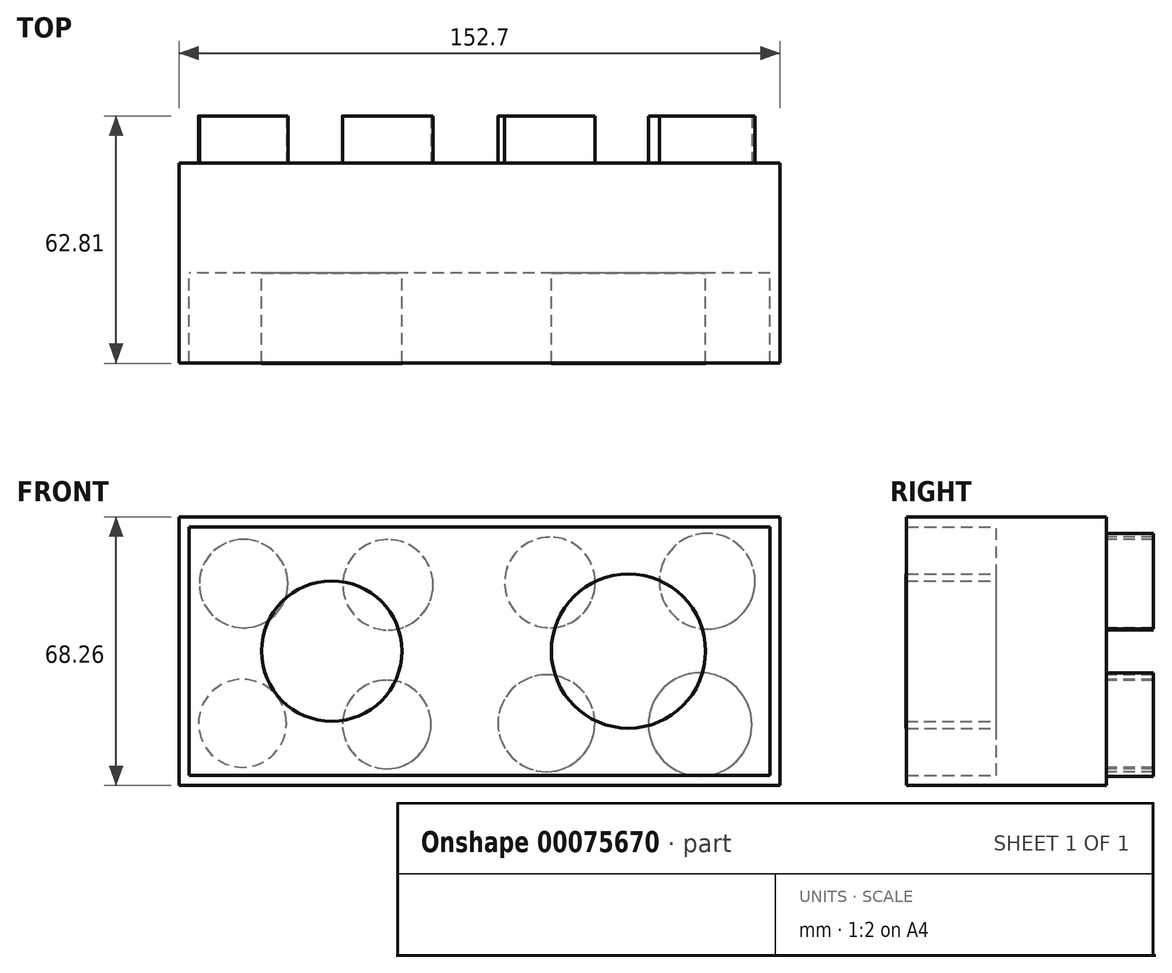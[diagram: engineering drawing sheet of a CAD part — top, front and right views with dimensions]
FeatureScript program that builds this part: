
annotation { "Feature Type Name" : "Feature", "Feature Type Description" : "" }
export const myFeature = defineFeature(function(context is Context, id is Id, definition is map)
    precondition{}
    {
        {
            var Q0;
            Q0=qCreatedBy(makeId("Front.planeOp"),FACE);
            var sketch = newSketch(context, id + "F0", { "sketchPlane" : qUnion([Q0])});
            skLineSegment(sketch, "E0.rect.bottom", {"start": v(76.35, -34.13) * mm, "end": v(-76.35, -34.13) * mm});
            skLineSegment(sketch, "E0.rect.top", {"start": v(76.35, 34.13) * mm, "end": v(-76.35, 34.13) * mm});
            skLineSegment(sketch, "E0.rect.left", {"start": v(76.35, -34.13) * mm, "end": v(76.35, 34.13) * mm});
            skLineSegment(sketch, "E0.rect.right", {"start": v(-76.35, -34.13) * mm, "end": v(-76.35, 34.13) * mm});
            skPoint(sketch, "E0.rect.middle", {"position": v(0, 0) * mm});
            skSolve(sketch);
        }
        {
            var Q0;
            Q0=makeQuery(id+"F0.imprint","IMPRINT",FACE,{"disambiguationData":[TD([[makeQuery(id+"F0.imprint","IMPRINT",EDGE,{"derivedFrom":sQuery(id+"F0.wireOp",EDGE,"E0.rect.bottom")}),-1.0]])]});
            extrude(context, id + "F1", {"entities" : qUnion([Q0]), "depth" : 25.4 * mm});
        }
        {
            var Q0;
            Q0=makeQuery(id+"F1.opExtrude","CAP_FACE",FACE,{"disambiguationData":[OSD([sQuery(id+"F0.wireOp",EDGE,"E0.rect.bottom"),sQuery(id+"F0.wireOp",EDGE,"E0.rect.top"),sQuery(id+"F0.wireOp",EDGE,"E0.rect.left"),sQuery(id+"F0.wireOp",EDGE,"E0.rect.right")])],"isStart":false});
            extrude(context, id + "F2", {"entities" : qUnion([Q0]), "operationType" : NewBodyOperationType.ADD, "depth" : 25.4 * mm});
        }
        {
            var Q0;
            Q0=makeQuery(id+"F2.opExtrude","CAP_FACE",FACE,{"disambiguationData":[OSD([sQuery(id+"F0.wireOp",EDGE,"E0.rect.bottom"),sQuery(id+"F0.wireOp",EDGE,"E0.rect.top"),sQuery(id+"F0.wireOp",EDGE,"E0.rect.left"),sQuery(id+"F0.wireOp",EDGE,"E0.rect.right")])],"isStart":false});
            shell(context, id + "F3", {"entities" : qUnion([Q0]), "thickness" : 2.54 * mm});
        }
        {
            var Q0;
            Q0=makeQuery(id+"F3.opShell","OFFSET_FACE",FACE,{"disambiguationData":[OSD([sQuery(id+"F0.wireOp",EDGE,"E0.rect.bottom"),sQuery(id+"F0.wireOp",EDGE,"E0.rect.top"),sQuery(id+"F0.wireOp",EDGE,"E0.rect.left"),sQuery(id+"F0.wireOp",EDGE,"E0.rect.right")])]});
            extrude(context, id + "F4", {"entities" : qUnion([Q0]), "operationType" : NewBodyOperationType.ADD, "depth" : 25.4 * mm});
        }
        {
            var Q0;
            Q0=makeQuery(id+"F1.opExtrude","CAP_FACE",FACE,{"disambiguationData":[OSD([sQuery(id+"F0.wireOp",EDGE,"E0.rect.bottom"),sQuery(id+"F0.wireOp",EDGE,"E0.rect.top"),sQuery(id+"F0.wireOp",EDGE,"E0.rect.left"),sQuery(id+"F0.wireOp",EDGE,"E0.rect.right")])],"isStart":true});
            var sketch = newSketch(context, id + "F5", { "sketchPlane" : qUnion([Q0])});
            skCircle(sketch, "E1", {"center": v(60.24, -18.34) * mm, "radius": 11.17 * mm});
            skCircle(sketch, "E2", {"center": v(23.56, -18.64) * mm, "radius": 11.25 * mm});
            skCircle(sketch, "E3", {"center": v(59.94, 17.15) * mm, "radius": 11.24 * mm});
            skCircle(sketch, "E4", {"center": v(23.26, 16.85) * mm, "radius": 11.47 * mm});
            skCircle(sketch, "E5", {"center": v(-17, -18.34) * mm, "radius": 12.3 * mm});
            skCircle(sketch, "E6", {"center": v(-56.06, -18.64) * mm, "radius": 13.13 * mm});
            skCircle(sketch, "E7", {"center": v(-17.9, 17.44) * mm, "radius": 11.5 * mm});
            skCircle(sketch, "E8", {"center": v(-57.85, 17.74) * mm, "radius": 12.17 * mm});
            skSolve(sketch);
        }
        {
            var Q0;
            Q0=makeQuery(id+"F5.imprint","IMPRINT",FACE,{"disambiguationData":[TD([[makeQuery(id+"F5.imprint","IMPRINT",EDGE,{"derivedFrom":sQuery(id+"F5.wireOp",EDGE,"E1")}),1.0]])]});
            var Q1;
            Q1=makeQuery(id+"F5.imprint","IMPRINT",FACE,{"disambiguationData":[TD([[makeQuery(id+"F5.imprint","IMPRINT",EDGE,{"derivedFrom":sQuery(id+"F5.wireOp",EDGE,"E2")}),1.0]])]});
            var Q2;
            Q2=makeQuery(id+"F5.imprint","IMPRINT",FACE,{"disambiguationData":[TD([[makeQuery(id+"F5.imprint","IMPRINT",EDGE,{"derivedFrom":sQuery(id+"F5.wireOp",EDGE,"E5")}),1.0]])]});
            var Q3;
            Q3=makeQuery(id+"F5.imprint","IMPRINT",FACE,{"disambiguationData":[TD([[makeQuery(id+"F5.imprint","IMPRINT",EDGE,{"derivedFrom":sQuery(id+"F5.wireOp",EDGE,"E6")}),1.0]])]});
            var Q4;
            Q4=makeQuery(id+"F5.imprint","IMPRINT",FACE,{"disambiguationData":[TD([[makeQuery(id+"F5.imprint","IMPRINT",EDGE,{"derivedFrom":sQuery(id+"F5.wireOp",EDGE,"E8")}),1.0]])]});
            var Q5;
            Q5=makeQuery(id+"F5.imprint","IMPRINT",FACE,{"disambiguationData":[TD([[makeQuery(id+"F5.imprint","IMPRINT",EDGE,{"derivedFrom":sQuery(id+"F5.wireOp",EDGE,"E7")}),1.0]])]});
            var Q6;
            Q6=makeQuery(id+"F5.imprint","IMPRINT",FACE,{"disambiguationData":[TD([[makeQuery(id+"F5.imprint","IMPRINT",EDGE,{"derivedFrom":sQuery(id+"F5.wireOp",EDGE,"E4")}),1.0]])]});
            var Q7;
            Q7=makeQuery(id+"F5.imprint","IMPRINT",FACE,{"disambiguationData":[TD([[makeQuery(id+"F5.imprint","IMPRINT",EDGE,{"derivedFrom":sQuery(id+"F5.wireOp",EDGE,"E3")}),1.0]])]});
            extrude(context, id + "F6", {"entities" : qUnion([Q0, Q1, Q2, Q3, Q4, Q5, Q6, Q7]), "operationType" : NewBodyOperationType.ADD, "depth" : 11.9 * mm});
        }
        {
            var Q0;
            Q0=makeQuery(id+"F5.imprint","IMPRINT",FACE,{"disambiguationData":[TD([[makeQuery(id+"F5.imprint","IMPRINT",EDGE,{"derivedFrom":sQuery(id+"F5.wireOp",EDGE,"E1")}),1.0]])]});
            var Q1;
            Q1=makeQuery(id+"F5.imprint","IMPRINT",FACE,{"disambiguationData":[TD([[makeQuery(id+"F5.imprint","IMPRINT",EDGE,{"derivedFrom":sQuery(id+"F5.wireOp",EDGE,"E2")}),1.0]])]});
            var Q2;
            Q2=makeQuery(id+"F5.imprint","IMPRINT",FACE,{"disambiguationData":[TD([[makeQuery(id+"F5.imprint","IMPRINT",EDGE,{"derivedFrom":sQuery(id+"F5.wireOp",EDGE,"E3")}),1.0]])]});
            var Q3;
            Q3=makeQuery(id+"F5.imprint","IMPRINT",FACE,{"disambiguationData":[TD([[makeQuery(id+"F5.imprint","IMPRINT",EDGE,{"derivedFrom":sQuery(id+"F5.wireOp",EDGE,"E4")}),1.0]])]});
            var Q4;
            Q4=makeQuery(id+"F5.imprint","IMPRINT",FACE,{"disambiguationData":[TD([[makeQuery(id+"F5.imprint","IMPRINT",EDGE,{"derivedFrom":sQuery(id+"F5.wireOp",EDGE,"E5")}),1.0]])]});
            var Q5;
            Q5=makeQuery(id+"F5.imprint","IMPRINT",FACE,{"disambiguationData":[TD([[makeQuery(id+"F5.imprint","IMPRINT",EDGE,{"derivedFrom":sQuery(id+"F5.wireOp",EDGE,"E6")}),1.0]])]});
            var Q6;
            Q6=makeQuery(id+"F5.imprint","IMPRINT",FACE,{"disambiguationData":[TD([[makeQuery(id+"F5.imprint","IMPRINT",EDGE,{"derivedFrom":sQuery(id+"F5.wireOp",EDGE,"E7")}),1.0]])]});
            var Q7;
            Q7=makeQuery(id+"F5.imprint","IMPRINT",FACE,{"disambiguationData":[TD([[makeQuery(id+"F5.imprint","IMPRINT",EDGE,{"derivedFrom":sQuery(id+"F5.wireOp",EDGE,"E8")}),1.0]])]});
            extrude(context, id + "F7", {"entities" : qUnion([Q0, Q1, Q2, Q3, Q4, Q5, Q6, Q7]), "operationType" : NewBodyOperationType.ADD, "depth" : 9.6 * mm});
        }
        {
            var Q0;
            Q0=makeQuery(id+"F4.opExtrude","CAP_FACE",FACE,{"disambiguationData":[OSD([sQuery(id+"F0.wireOp",EDGE,"E0.rect.bottom"),sQuery(id+"F0.wireOp",EDGE,"E0.rect.top"),sQuery(id+"F0.wireOp",EDGE,"E0.rect.left"),sQuery(id+"F0.wireOp",EDGE,"E0.rect.right")])],"isStart":false});
            var sketch = newSketch(context, id + "F8", { "sketchPlane" : qUnion([Q0])});
            skCircle(sketch, "E9", {"center": v(-37.55, 0) * mm, "radius": 17.82 * mm});
            skCircle(sketch, "E10", {"center": v(37.84, 0) * mm, "radius": 19.59 * mm});
            skSolve(sketch);
        }
        {
            var Q0;
            Q0=makeQuery(id+"F8.imprint","IMPRINT",FACE,{"disambiguationData":[TD([[makeQuery(id+"F8.imprint","IMPRINT",EDGE,{"derivedFrom":sQuery(id+"F8.wireOp",EDGE,"E9")}),1.0]])]});
            var Q1;
            Q1=makeQuery(id+"F8.imprint","IMPRINT",FACE,{"disambiguationData":[TD([[makeQuery(id+"F8.imprint","IMPRINT",EDGE,{"derivedFrom":sQuery(id+"F8.wireOp",EDGE,"E10")}),1.0]])]});
            extrude(context, id + "F9", {"entities" : qUnion([Q0, Q1]), "operationType" : NewBodyOperationType.ADD, "depth" : 22.97 * mm});
        }
    });
